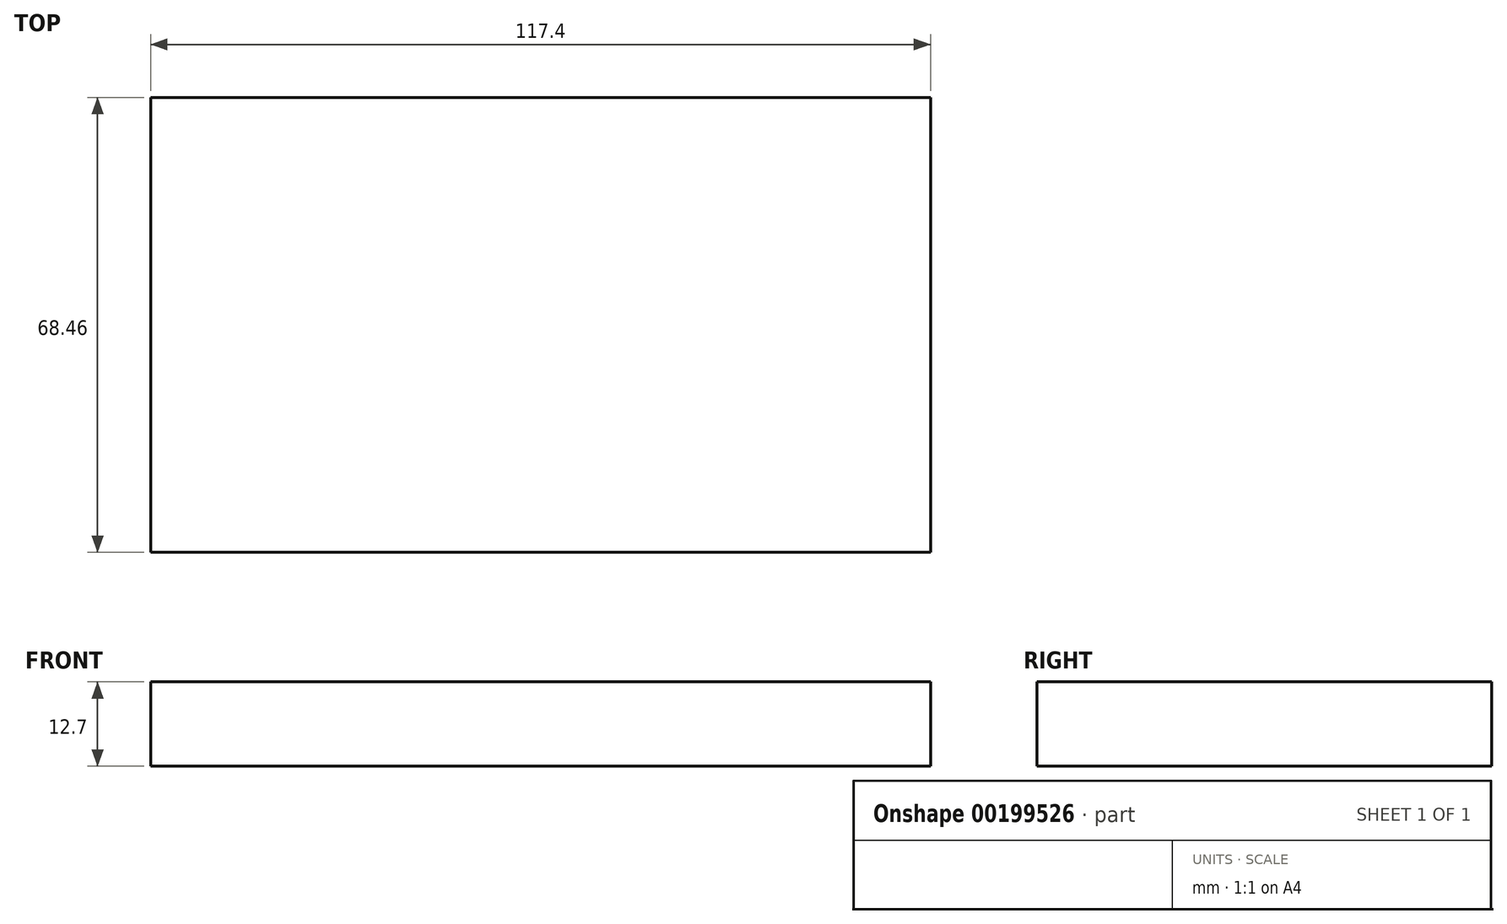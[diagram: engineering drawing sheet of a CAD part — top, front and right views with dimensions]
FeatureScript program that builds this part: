
annotation { "Feature Type Name" : "Feature", "Feature Type Description" : "" }
export const myFeature = defineFeature(function(context is Context, id is Id, definition is map)
    precondition{}
    {
        {
            var Q0;
            Q0=qCreatedBy(makeId("Top.planeOp"),FACE);
            var sketch = newSketch(context, id + "F0", { "sketchPlane" : qUnion([Q0])});
            skLineSegment(sketch, "E0.bottom", {"start": v(-66.55, -38.83) * mm, "end": v(50.85, -38.83) * mm});
            skLineSegment(sketch, "E0.top", {"start": v(-66.55, 29.63) * mm, "end": v(50.85, 29.63) * mm});
            skLineSegment(sketch, "E0.left", {"start": v(-66.55, -38.83) * mm, "end": v(-66.55, 29.63) * mm});
            skLineSegment(sketch, "E0.right", {"start": v(50.85, -38.83) * mm, "end": v(50.85, 29.63) * mm});
            skSolve(sketch);
        }
        {
            var Q0;
            Q0=makeQuery(id+"F0.imprint","IMPRINT",FACE,{"disambiguationData":[TD([[makeQuery(id+"F0.imprint","IMPRINT",EDGE,{"derivedFrom":sQuery(id+"F0.wireOp",EDGE,"E0.bottom")}),1.0]])]});
            extrude(context, id + "F1", {"entities" : qUnion([Q0]), "depth" : 12.7 * mm});
        }
    });
